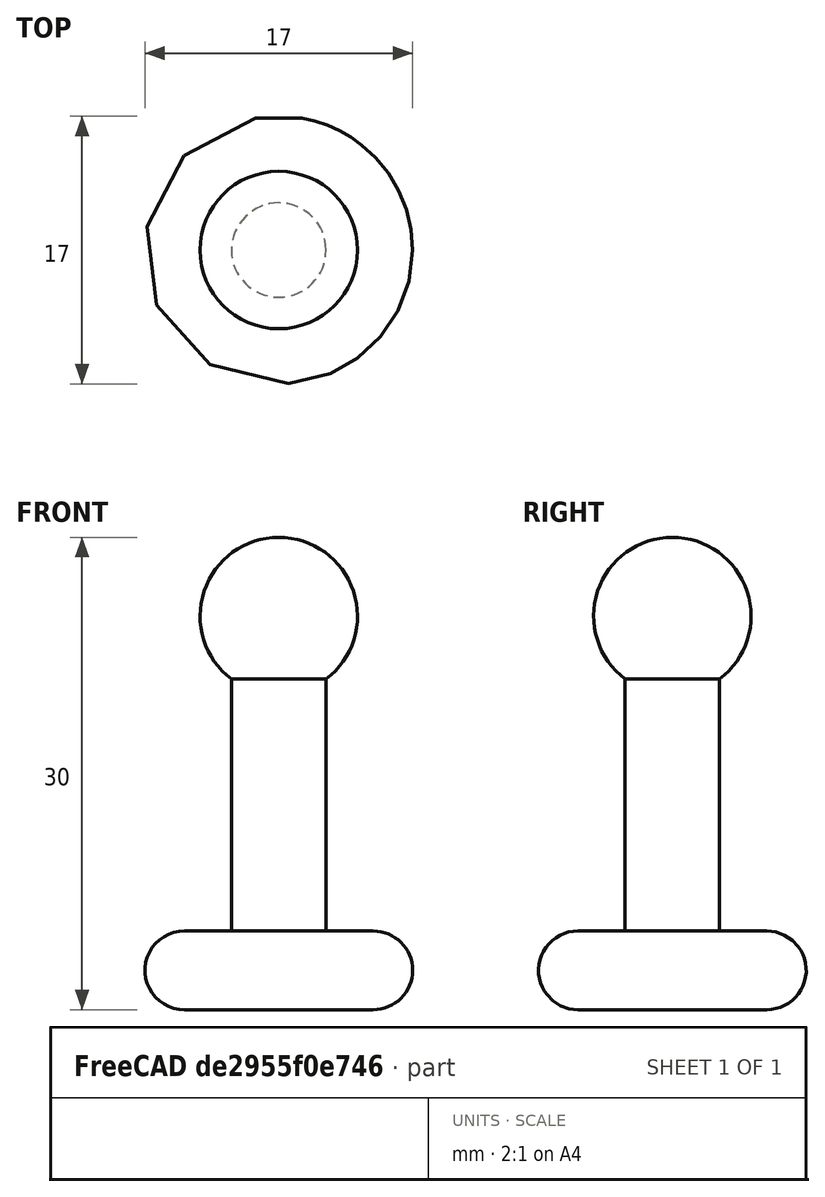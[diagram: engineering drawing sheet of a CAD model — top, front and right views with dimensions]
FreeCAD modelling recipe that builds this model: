
FCSTD DOCUMENT  (FreeCAD 0.15R4641 (Git))
Label: pawn-v002
License: All rights reserved
LicenseURL: http://en.wikipedia.org/wiki/All_rights_reserved
objects: Sketcher::SketchObject×1, PartDesign::Revolution×1
note: 3 computed .brp shape members not serialized (recipe doc carries the construction recipe); baked Part::Feature solids carry a one-line shape summary decoded from their .brp

FEATURE [Sketcher::SketchObject] Sketch
  Placement = pos=(0,0,0) rot=(-1,0,0;4.71239rad)
  sketch-geometry (9):
    g0: LineSegment StartX=0 StartY=0 StartZ=0 EndX=6 EndY=0 EndZ=0
    g1: LineSegment [constr] StartX=6 StartY=0 StartZ=0 EndX=6 EndY=5 EndZ=0
    g2: LineSegment StartX=6 StartY=5 StartZ=0 EndX=0 EndY=5 EndZ=0
    g3: LineSegment StartX=0 StartY=5 StartZ=0 EndX=0 EndY=0 EndZ=0
    g4: LineSegment StartX=0 StartY=5 StartZ=0 EndX=3 EndY=5 EndZ=0
    g5: LineSegment StartX=3 StartY=5 StartZ=0 EndX=3 EndY=21 EndZ=0
    g6: ArcOfCircle CenterX=6 CenterY=2.5 CenterZ=0 NormalX=0 NormalY=0 NormalZ=1 Radius=2.5 StartAngle=4.71239 EndAngle=7.85398
    g7: ArcOfCircle CenterX=0 CenterY=25 CenterZ=0 NormalX=0 NormalY=0 NormalZ=1 Radius=5 StartAngle=5.35589 EndAngle=7.85398
    g8: LineSegment StartX=0 StartY=5 StartZ=0 EndX=0 EndY=30 EndZ=0
  constraints (26):
    c: Coincident(g0,g1)
    c: Coincident(g1,g2)
    c: Coincident(g2,g3)
    c: Coincident(g3,g0)
    c: Horizontal(g0)
    c: Horizontal(g2)
    c: Vertical(g1)
    c: Vertical(g3)
    c: Coincident(g0,g-1)
    c: Coincident(g4,g5)
    c: Horizontal(g4)
    c: Vertical(g5)
    c: Coincident(g4,g2)
    c: DistanceX(g0) = 6
    c: DistanceY(g1) = 5
    c: Coincident(g6,g1)
    c: Coincident(g6,g0)
    c: PointOnObject(g6,g1)
    c: PointOnObject(g7,g-2)
    c: Radius(g7) = 5
    c: Coincident(g5,g7)
    c: DistanceX(g4,g2) = -3
    c: Coincident(g8,g2)
    c: Coincident(g8,g7)
    c: Perpendicular(g7,g8)
    c: DistanceY(g-1,g7) = 25
FEATURE [PartDesign::Revolution] Revolution
  Angle = 360
  Axis = (0,0,1)
  Base = (0,0,0)
  Placement = pos=(0,0,0) rot=(-1,0,0;4.71239rad)
  ReferenceAxis = -> Sketch [V_Axis]
  Reversed = true
  Sketch = -> Sketch
